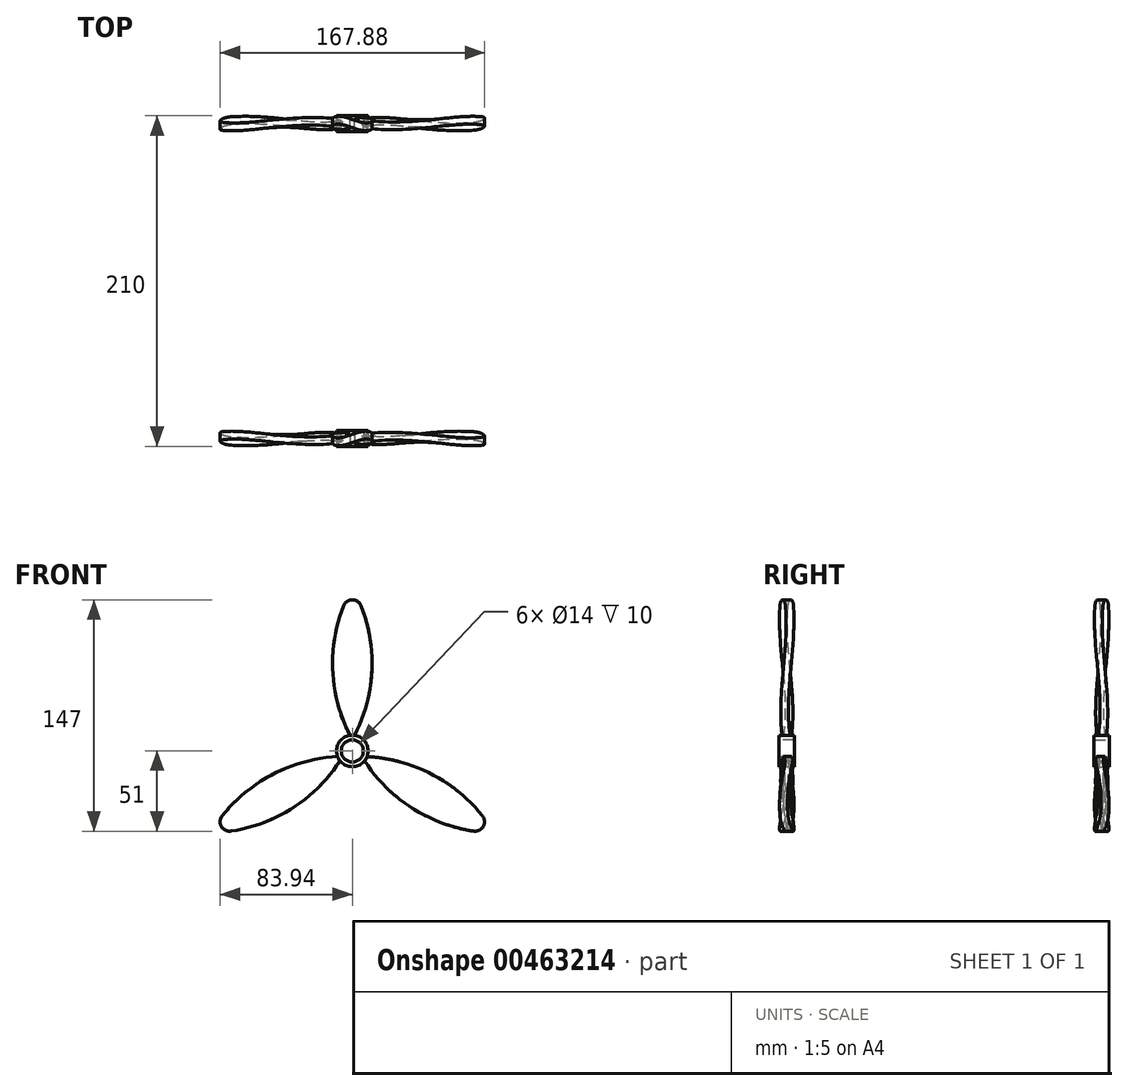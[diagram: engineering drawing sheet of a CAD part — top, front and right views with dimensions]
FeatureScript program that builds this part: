
annotation { "Feature Type Name" : "Feature", "Feature Type Description" : "" }
export const myFeature = defineFeature(function(context is Context, id is Id, definition is map)
    precondition{}
    {
        {
            var Q0;
            Q0=qCreatedBy(makeId("Top.planeOp"),FACE);
            cPlane(context, id + "F0", {"entities" : qUnion([Q0]), "cplaneType" : CPlaneType.OFFSET, "offset" : 100 * mm, "width" : 150 * mm, "height" : 150 * mm});
        }
        {
            var Q0;
            Q0=qCreatedBy(makeId("Top.planeOp"),FACE);
            var sketch = newSketch(context, id + "F1", { "sketchPlane" : qUnion([Q0])});
            skLineSegment(sketch, "E0", {"start": v(-24.35, -6.2) * mm, "end": v(22.64, 10.9) * mm});
            skLineSegment(sketch, "E1", {"start": v(22.64, 10.9) * mm, "end": v(24.35, 6.2) * mm});
            skLineSegment(sketch, "E2", {"start": v(24.35, 6.2) * mm, "end": v(-22.64, -10.9) * mm});
            skLineSegment(sketch, "E3", {"start": v(-22.64, -10.9) * mm, "end": v(-24.35, -6.2) * mm});
            skLineSegment(sketch, "E4", {"start": v(0, -23) * mm, "end": v(0, 33.25) * mm, "construction": true});
            skLineSegment(sketch, "E5", {"start": v(-38.5, 0) * mm, "end": v(35.25, 0) * mm, "construction": true});
            skLineSegment(sketch, "E6", {"start": v(23.5, 8.55) * mm, "end": v(-23.5, -8.55) * mm, "construction": true});
            skLineSegment(sketch, "E7", {"start": v(-0.86, 2.35) * mm, "end": v(0.86, -2.35) * mm, "construction": true});
            skSolve(sketch);
        }
        {
            var Q0;
            Q0=qCreatedBy(id+"F0.planeOp",FACE);
            var sketch = newSketch(context, id + "F2", { "sketchPlane" : qUnion([Q0])});
            skLineSegment(sketch, "E8", {"start": v(-22.63, 10.92) * mm, "end": v(24.35, -6.18) * mm});
            skLineSegment(sketch, "E9", {"start": v(24.35, -6.18) * mm, "end": v(22.64, -10.88) * mm});
            skLineSegment(sketch, "E10", {"start": v(22.64, -10.88) * mm, "end": v(-24.37, 6.23) * mm});
            skLineSegment(sketch, "E11", {"start": v(-24.37, 6.23) * mm, "end": v(-22.63, 10.92) * mm});
            skLineSegment(sketch, "E12", {"start": v(-23.5, 8.57) * mm, "end": v(23.5, -8.53) * mm, "construction": true});
            skLineSegment(sketch, "E13", {"start": v(0.86, 2.37) * mm, "end": v(-0.86, -2.37) * mm, "construction": true});
            skPoint(sketch, "E13.endSnap0", {"position": v(-0.86, -2.33) * mm});
            skSolve(sketch);
        }
        {
            var Q0;
            Q0=makeQuery(id+"F2.imprint","IMPRINT",FACE,{"disambiguationData":[TD([[makeQuery(id+"F2.imprint","IMPRINT",EDGE,{"derivedFrom":sQuery(id+"F2.wireOp",EDGE,"E8")}),-1.0]])]});
            var Q1;
            Q1=makeQuery(id+"F1.imprint","IMPRINT",FACE,{"disambiguationData":[TD([[makeQuery(id+"F1.imprint","IMPRINT",EDGE,{"derivedFrom":sQuery(id+"F1.wireOp",EDGE,"E0")}),-1.0]])]});
            loft(context, id + "F3", {"sheetProfilesArray" : [{ "sheetProfileEntities" : qUnion([Q0]) }, { "sheetProfileEntities" : qUnion([Q1]) }]});
        }
        {
            var Q0;
            Q0=qCreatedBy(makeId("Front.planeOp"),FACE);
            var sketch = newSketch(context, id + "F4", { "sketchPlane" : qUnion([Q0])});
            skLineSegment(sketch, "E14", {"start": v(0, 0) * mm, "end": v(0, 37.38) * mm, "construction": true});
            skArc(sketch, "E15", {"start": v(0, 7) * mm, "mid": v(12.34, 48.98) * mm, "end": v(5.58, 92.2) * mm});
            skArc(sketch, "E16", {"start": v(5.58, 92.2) * mm, "mid": v(3.38, 94.96) * mm, "end": v(0, 96) * mm});
            skArc(sketch, "E17.MirrorCS", {"start": v(0, 7) * mm, "mid": v(-12.34, 48.98) * mm, "end": v(-5.58, 92.2) * mm});
            skArc(sketch, "E18.MirrorCS", {"start": v(-5.58, 92.2) * mm, "mid": v(-3.38, 94.96) * mm, "end": v(0, 96) * mm});
            skSolve(sketch);
        }
        {
            var Q0;
            Q0 = qSketchRegion(id + "F4", true);
            extrude(context, id + "F5", {"entities" : qUnion([Q0]), "operationType" : NewBodyOperationType.INTERSECT, "endBound" : BoundingType.SYMMETRIC, "depth" : 10 * mm});
        }
        {
            var Q0;
            Q0=qCreatedBy(makeId("Front.planeOp"),FACE);
            var sketch = newSketch(context, id + "F6", { "sketchPlane" : qUnion([Q0])});
            skCircle(sketch, "E19", {"center": v(0, 0) * mm, "radius": 7 * mm});
            skCircle(sketch, "E20", {"center": v(0, 0) * mm, "radius": 10 * mm});
            skSolve(sketch);
        }
        {
            var Q0;
            Q0 = qSketchRegion(id + "F6", true);
            extrude(context, id + "F7", {"entities" : qUnion([Q0]), "operationType" : NewBodyOperationType.ADD, "endBound" : BoundingType.SYMMETRIC, "depth" : 10 * mm});
        }
        {
            var Q0;
            Q0=makeQuery(id+"F3.opLoft","SWEPT_BODY",BODY,{"disambiguationData":[OSD([makeQuery(id+"F1.imprint","IMPRINT",FACE,{"disambiguationData":[TD([[makeQuery(id+"F1.imprint","IMPRINT",EDGE,{"derivedFrom":sQuery(id+"F1.wireOp",EDGE,"E0")}),-1.0]])]}),makeQuery(id+"F2.imprint","IMPRINT",FACE,{"disambiguationData":[TD([[makeQuery(id+"F2.imprint","IMPRINT",EDGE,{"derivedFrom":sQuery(id+"F2.wireOp",EDGE,"E8")}),-1.0]])]})])]});
            var Q1;
            Q1=makeQuery(id+"F7.opExtrude","CAP_EDGE",EDGE,{"disambiguationData":[OSD([sQuery(id+"F6.wireOp",EDGE,"E20")])],"isStart":false});
            circularPattern(context, id + "F8", {"entities" : qUnion([Q0]), "axis" : qUnion([Q1]), "angle" : 360 * degree, "instanceCount" : 3, "equalSpace" : true});
        }
        {
            var Q0;
            Q0=qCreatedBy(makeId("Front.planeOp"),FACE);
            cPlane(context, id + "F9", {"entities" : qUnion([Q0]), "cplaneType" : CPlaneType.OFFSET, "offset" : 100 * mm, "width" : 150 * mm, "height" : 150 * mm});
        }
        {
            var Q0;
            Q0=makeQuery(id+"F3.opLoft","SWEPT_BODY",BODY,{"disambiguationData":[OSD([makeQuery(id+"F1.imprint","IMPRINT",FACE,{"disambiguationData":[TD([[makeQuery(id+"F1.imprint","IMPRINT",EDGE,{"derivedFrom":sQuery(id+"F1.wireOp",EDGE,"E0")}),-1.0]])]}),makeQuery(id+"F2.imprint","IMPRINT",FACE,{"disambiguationData":[TD([[makeQuery(id+"F2.imprint","IMPRINT",EDGE,{"derivedFrom":sQuery(id+"F2.wireOp",EDGE,"E8")}),-1.0]])]})])]});
            var Q1;
            Q1=makeQuery(id+"F8.opPattern","COPY",BODY,{"derivedFrom":makeQuery(id+"F3.opLoft","SWEPT_BODY",BODY,{"disambiguationData":[OSD([makeQuery(id+"F1.imprint","IMPRINT",FACE,{"disambiguationData":[TD([[makeQuery(id+"F1.imprint","IMPRINT",EDGE,{"derivedFrom":sQuery(id+"F1.wireOp",EDGE,"E0")}),-1.0]])]}),makeQuery(id+"F2.imprint","IMPRINT",FACE,{"disambiguationData":[TD([[makeQuery(id+"F2.imprint","IMPRINT",EDGE,{"derivedFrom":sQuery(id+"F2.wireOp",EDGE,"E8")}),-1.0]])]})])]}),"instanceName":"2"});
            var Q2;
            Q2=makeQuery(id+"F8.opPattern","COPY",BODY,{"derivedFrom":makeQuery(id+"F3.opLoft","SWEPT_BODY",BODY,{"disambiguationData":[OSD([makeQuery(id+"F1.imprint","IMPRINT",FACE,{"disambiguationData":[TD([[makeQuery(id+"F1.imprint","IMPRINT",EDGE,{"derivedFrom":sQuery(id+"F1.wireOp",EDGE,"E0")}),-1.0]])]}),makeQuery(id+"F2.imprint","IMPRINT",FACE,{"disambiguationData":[TD([[makeQuery(id+"F2.imprint","IMPRINT",EDGE,{"derivedFrom":sQuery(id+"F2.wireOp",EDGE,"E8")}),-1.0]])]})])]}),"instanceName":"1"});
            var Q3;
            Q3=qCreatedBy(id+"F9.planeOp",FACE);
            mirror(context, id + "F10", {"entities" : qUnion([Q0, Q1, Q2]), "mirrorPlane" : qUnion([Q3])});
        }
    });
